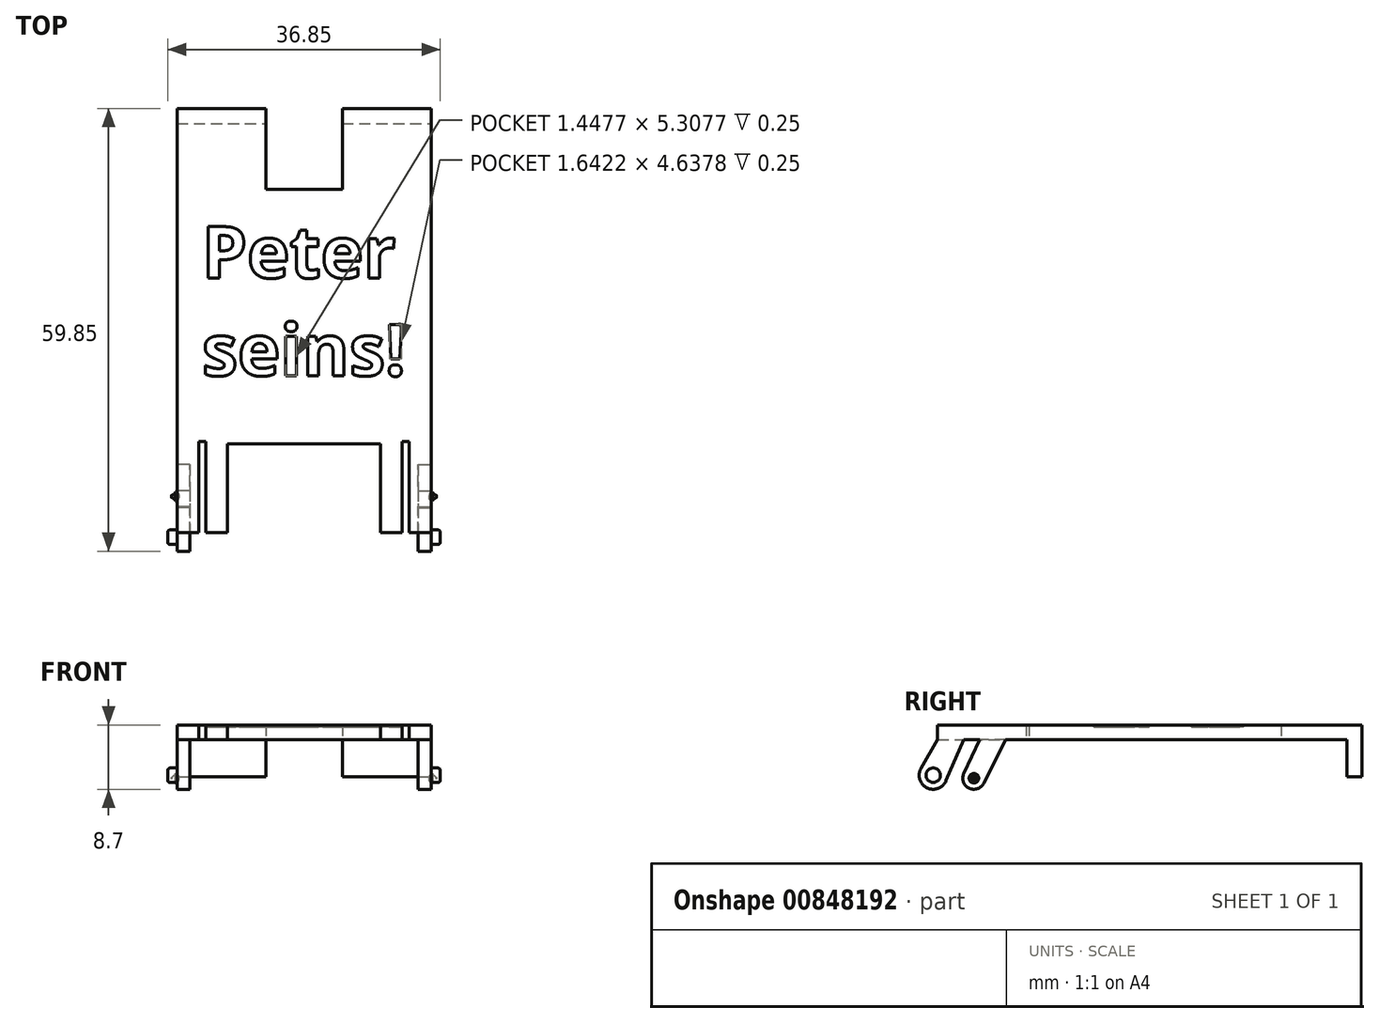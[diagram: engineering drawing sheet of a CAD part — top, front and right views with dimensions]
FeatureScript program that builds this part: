
annotation { "Feature Type Name" : "Feature", "Feature Type Description" : "" }
export const myFeature = defineFeature(function(context is Context, id is Id, definition is map)
    precondition{}
    {
        {
            var Q0;
            Q0=qCreatedBy(makeId("Right.planeOp"),FACE);
            var sketch = newSketch(context, id + "F0", { "sketchPlane" : qUnion([Q0])});
            skLineSegment(sketch, "E0.bottom", {"start": v(25.06, 0) * mm, "end": v(-32.3, 0) * mm});
            skLineSegment(sketch, "E0.top", {"start": v(25.06, -2) * mm, "end": v(-32.3, -2) * mm});
            skLineSegment(sketch, "E0.left", {"start": v(25.06, 0) * mm, "end": v(25.06, -2) * mm});
            skLineSegment(sketch, "E0.right", {"start": v(-32.3, 0) * mm, "end": v(-32.3, -2) * mm});
            skLineSegment(sketch, "E1.bottom", {"start": v(25.06, -2) * mm, "end": v(23.06, -2) * mm});
            skLineSegment(sketch, "E1.top", {"start": v(25.06, 5) * mm, "end": v(23.06, 5) * mm});
            skLineSegment(sketch, "E1.left", {"start": v(25.06, -2) * mm, "end": v(25.06, 5) * mm});
            skLineSegment(sketch, "E1.right", {"start": v(23.06, -2) * mm, "end": v(23.06, 5) * mm});
            skSolve(sketch);
        }
        {
            var Q0;
            Q0 = qSketchRegion(id + "F0", true);
            extrude(context, id + "F1", {"entities" : qUnion([Q0]), "depth" : 34.35 * mm, "offsetDistance" : 25 * mm});
        }
        {
            var Q0;
            Q0=qCreatedBy(makeId("Top.planeOp"),FACE);
            var sketch = newSketch(context, id + "F2", { "sketchPlane" : qUnion([Q0])});
            skLineSegment(sketch, "E2.bottom", {"start": v(6.85, -20.3) * mm, "end": v(27.5, -20.3) * mm});
            skLineSegment(sketch, "E2.top", {"start": v(6.85, -32.4) * mm, "end": v(27.5, -32.4) * mm});
            skLineSegment(sketch, "E2.left", {"start": v(6.85, -20.3) * mm, "end": v(6.85, -32.4) * mm});
            skLineSegment(sketch, "E2.right", {"start": v(27.5, -20.3) * mm, "end": v(27.5, -32.4) * mm});
            skLineSegment(sketch, "E3.bottom", {"start": v(12, 25.16) * mm, "end": v(22.35, 25.16) * mm});
            skLineSegment(sketch, "E3.top", {"start": v(12, 14.16) * mm, "end": v(22.35, 14.16) * mm});
            skLineSegment(sketch, "E3.left", {"start": v(12, 25.16) * mm, "end": v(12, 14.16) * mm});
            skLineSegment(sketch, "E3.right", {"start": v(22.35, 25.16) * mm, "end": v(22.35, 14.16) * mm});
            skLineSegment(sketch, "E4.bottom", {"start": v(2.93, -19.93) * mm, "end": v(3.93, -19.93) * mm});
            skLineSegment(sketch, "E4.top", {"start": v(2.93, -34.8) * mm, "end": v(3.93, -34.8) * mm});
            skLineSegment(sketch, "E4.left", {"start": v(2.93, -19.93) * mm, "end": v(2.93, -34.8) * mm});
            skLineSegment(sketch, "E4.right", {"start": v(3.93, -19.93) * mm, "end": v(3.93, -34.8) * mm});
            skLineSegment(sketch, "E5", {"start": v(17.18, 25.16) * mm, "end": v(17.18, -32.4) * mm, "construction": true});
            skLineSegment(sketch, "E6.MirrorCS", {"start": v(31.43, -19.93) * mm, "end": v(31.43, -34.8) * mm});
            skLineSegment(sketch, "E7.MirrorCS", {"start": v(30.43, -19.93) * mm, "end": v(30.43, -34.8) * mm});
            skLineSegment(sketch, "E8.MirrorCS", {"start": v(31.43, -19.93) * mm, "end": v(30.42, -19.93) * mm});
            skLineSegment(sketch, "E9.MirrorCS", {"start": v(31.43, -34.8) * mm, "end": v(30.42, -34.8) * mm});
            skSolve(sketch);
        }
        {
            var Q0;
            Q0=makeQuery(id+"F2.imprint","IMPRINT",FACE,{"disambiguationData":[TD([[makeQuery(id+"F2.imprint","IMPRINT",EDGE,{"derivedFrom":sQuery(id+"F2.wireOp",EDGE,"E2.bottom")}),-1.0]])]});
            var Q1;
            Q1=makeQuery(id+"F2.imprint","IMPRINT",FACE,{"disambiguationData":[TD([[makeQuery(id+"F2.imprint","IMPRINT",EDGE,{"derivedFrom":sQuery(id+"F2.wireOp",EDGE,"E3.bottom")}),-1.0]])]});
            var Q2;
            Q2=makeQuery(id+"F2.imprint","IMPRINT",FACE,{"disambiguationData":[TD([[makeQuery(id+"F2.imprint","IMPRINT",EDGE,{"derivedFrom":sQuery(id+"F2.wireOp",EDGE,"E4.bottom")}),-1.0]])]});
            var Q3;
            Q3=makeQuery(id+"F2.imprint","IMPRINT",FACE,{"disambiguationData":[TD([[makeQuery(id+"F2.imprint","IMPRINT",EDGE,{"derivedFrom":sQuery(id+"F2.wireOp",EDGE,"E6.MirrorCS")}),-1.0]])]});
            extrude(context, id + "F3", {"entities" : qUnion([Q0, Q1, Q2, Q3]), "operationType" : NewBodyOperationType.REMOVE, "endBound" : BoundingType.SYMMETRIC, "oppositeDirection" : true, "depth" : 25 * mm, "offsetDistance" : 25 * mm});
        }
        {
            var Q0;
            Q0=qCreatedBy(makeId("Right.planeOp"),FACE);
            var sketch = newSketch(context, id + "F4", { "sketchPlane" : qUnion([Q0])});
            skCircle(sketch, "E10", {"center": v(-32.9, 4.8) * mm, "radius": 1.9 * mm});
            skLineSegment(sketch, "E11", {"start": v(-34.53, 3.84) * mm, "end": v(-32.3, 0) * mm});
            skLineSegment(sketch, "E12", {"start": v(-32.3, 0) * mm, "end": v(-28.8, 0) * mm});
            skLineSegment(sketch, "E13", {"start": v(-28.8, 0) * mm, "end": v(-31.14, 5.54) * mm});
            skCircle(sketch, "E14", {"center": v(-32.9, 4.8) * mm, "radius": 1.9 * mm, "construction": true});
            skCircle(sketch, "E15", {"center": v(-27.4, 5.2) * mm, "radius": 1.5 * mm});
            skLineSegment(sketch, "E16", {"start": v(-26.05, 5.87) * mm, "end": v(-23.1, 0) * mm});
            skLineSegment(sketch, "E17", {"start": v(-23.1, 0) * mm, "end": v(-26.6, 0) * mm});
            skLineSegment(sketch, "E18", {"start": v(-26.6, 0) * mm, "end": v(-28.75, 4.56) * mm});
            skCircle(sketch, "E19", {"center": v(-27.4, 5.2) * mm, "radius": 1.5 * mm, "construction": true});
            skSolve(sketch);
        }
        {
            var Q0;
            {var subQ0=sQuery(id+"F4.wireOp",EDGE,"E15");var subQ1=makeQuery(id+"F4.imprint","INTERSECT",VERTEX,{"derivedFrom":[subQ0,sQuery(id+"F4.wireOp",EDGE,"E16")]});Q0=makeQuery(id+"F4.imprint","IMPRINT",FACE,{"disambiguationData":[TD([[makeQuery(id+"F4.imprint","IMPRINT",EDGE,{"disambiguationData":[TD([[subQ1,-1.0]])],"derivedFrom":subQ0}),1.0]])]});}
            var Q1;
            {var subQ0=sQuery(id+"F4.wireOp",EDGE,"E16");Q1=makeQuery(id+"F4.imprint","IMPRINT",FACE,{"disambiguationData":[TD([[makeQuery(id+"F4.imprint","IMPRINT",EDGE,{"derivedFrom":subQ0}),-1.0]])]});}
            var Q2;
            {var subQ0=sQuery(id+"F4.wireOp",EDGE,"E11");Q2=makeQuery(id+"F4.imprint","IMPRINT",FACE,{"disambiguationData":[TD([[makeQuery(id+"F4.imprint","IMPRINT",EDGE,{"derivedFrom":subQ0}),1.0]])]});}
            var Q3;
            {var subQ0=sQuery(id+"F4.wireOp",EDGE,"E10");var subQ1=makeQuery(id+"F4.imprint","INTERSECT",VERTEX,{"derivedFrom":[subQ0,sQuery(id+"F4.wireOp",EDGE,"E11")]});Q3=makeQuery(id+"F4.imprint","IMPRINT",FACE,{"disambiguationData":[TD([[makeQuery(id+"F4.imprint","IMPRINT",EDGE,{"disambiguationData":[TD([[subQ1,1.0]])],"derivedFrom":subQ0}),1.0]])]});}
            extrude(context, id + "F5", {"entities" : qUnion([Q0, Q1, Q2, Q3]), "depth" : 1.75 * mm, "offsetDistance" : 25 * mm});
        }
        {
            var Q0;
            Q0=qCreatedBy(makeId("Right.planeOp"),FACE);
            var sketch = newSketch(context, id + "F6", { "sketchPlane" : qUnion([Q0])});
            skCircle(sketch, "E20", {"center": v(-32.9, 4.8) * mm, "radius": 0.98 * mm});
            skSolve(sketch);
        }
        {
            var Q0;
            Q0=makeQuery(id+"F6.imprint","IMPRINT",FACE,{"disambiguationData":[TD([[makeQuery(id+"F6.imprint","IMPRINT",EDGE,{"derivedFrom":sQuery(id+"F6.wireOp",EDGE,"E20")}),1.0]])]});
            extrude(context, id + "F7", {"entities" : qUnion([Q0]), "oppositeDirection" : true, "depth" : 1.25 * mm, "offsetDistance" : 25 * mm});
        }
        {
            var Q0;
            Q0=qCreatedBy(makeId("Right.planeOp"),FACE);
            var sketch = newSketch(context, id + "F8", { "sketchPlane" : qUnion([Q0])});
            skCircle(sketch, "E21", {"center": v(-27.4, 5.2) * mm, "radius": 0.65 * mm});
            skSolve(sketch);
        }
        {
            var Q0;
            Q0=makeQuery(id+"F8.imprint","IMPRINT",FACE,{"disambiguationData":[TD([[makeQuery(id+"F8.imprint","IMPRINT",EDGE,{"derivedFrom":sQuery(id+"F8.wireOp",EDGE,"E21")}),1.0]])]});
            extrude(context, id + "F9", {"entities" : qUnion([Q0]), "oppositeDirection" : true, "depth" : 0.75 * mm, "offsetDistance" : 25 * mm});
        }
        {
            var Q0;
            Q0=makeQuery(id+"F9.opExtrude","CAP_EDGE",EDGE,{"disambiguationData":[OSD([sQuery(id+"F8.wireOp",EDGE,"E21")])],"isStart":false});
            fillet(context, id + "F10", {"entities" : qUnion([Q0]), "radius" : 0.5 * mm, "tangentPropagation" : true, "allowEdgeOverflow" : false});
        }
        {
            var Q0;
            Q0=makeQuery(id+"F7.opExtrude","CAP_EDGE",EDGE,{"disambiguationData":[OSD([sQuery(id+"F6.wireOp",EDGE,"E20")])],"isStart":false});
            fillet(context, id + "F11", {"entities" : qUnion([Q0]), "radius" : 0.3 * mm, "tangentPropagation" : true, "allowEdgeOverflow" : false});
        }
        {
            var Q0;
            Q0=qCreatedBy(makeId("Right.planeOp"),FACE);
            cPlane(context, id + "F12", {"entities" : qUnion([Q0]), "cplaneType" : CPlaneType.OFFSET, "offset" : (34.35 / 2) * mm, "width" : 150 * mm, "height" : 150 * mm});
        }
        {
            var Q0;
            Q0=makeQuery(id+"F9.opExtrude","SWEPT_BODY",BODY,{"disambiguationData":[OSD([sQuery(id+"F8.wireOp",EDGE,"E21")])]});
            var Q1;
            Q1=makeQuery(id+"F5.opExtrude","SWEPT_BODY",BODY,{"disambiguationData":[OSD([sQuery(id+"F4.wireOp",EDGE,"E15"),sQuery(id+"F4.wireOp",EDGE,"E16"),sQuery(id+"F4.wireOp",EDGE,"E17"),sQuery(id+"F4.wireOp",EDGE,"E18")])]});
            var Q2;
            Q2=makeQuery(id+"F7.opExtrude","SWEPT_BODY",BODY,{"disambiguationData":[OSD([sQuery(id+"F6.wireOp",EDGE,"E20")])]});
            var Q3;
            Q3=makeQuery(id+"F5.opExtrude","SWEPT_BODY",BODY,{"disambiguationData":[OSD([sQuery(id+"F4.wireOp",EDGE,"E10"),sQuery(id+"F4.wireOp",EDGE,"E11"),sQuery(id+"F4.wireOp",EDGE,"E12"),sQuery(id+"F4.wireOp",EDGE,"E13")])]});
            var Q4;
            Q4=qCreatedBy(id+"F12.planeOp",FACE);
            mirror(context, id + "F13", {"operationType" : NewBodyOperationType.ADD, "entities" : qUnion([Q0, Q1, Q2, Q3]), "mirrorPlane" : qUnion([Q4])});
        }
        {
            var Q0;
            Q0=makeQuery(id+"F1.opExtrude","SWEPT_BODY",BODY,{"disambiguationData":[OSD([sQuery(id+"F0.wireOp",EDGE,"E0.bottom"),sQuery(id+"F0.wireOp",EDGE,"E0.top"),sQuery(id+"F0.wireOp",EDGE,"E0.right"),sQuery(id+"F0.wireOp",EDGE,"E1.bottom"),sQuery(id+"F0.wireOp",EDGE,"E1.top"),sQuery(id+"F0.wireOp",EDGE,"E1.left"),sQuery(id+"F0.wireOp",EDGE,"E1.right")])]});
            var Q1;
            {var subQ0=sQuery(id+"F0.wireOp",EDGE,"E1.right");var subQ1=sQuery(id+"F0.wireOp",EDGE,"E0.bottom");Q1=makeQuery(id+"F13.boolean.opBoolean","SPLIT",EDGE,{"disambiguationData":[TD([makeQuery(id+"F1.opExtrude","SWEPT_FACE",FACE,{"disambiguationData":[OSD([subQ0])]})])],"derivedFrom":makeQuery(id+"F1.opExtrude","CAP_EDGE",EDGE,{"disambiguationData":[OSD([subQ1])],"isStart":true})});}
            transform(context, id + "F14", {"entities" : qUnion([Q0]), "transformType" : TransformType.ROTATION, "transformAxis" : qUnion([Q1]), "angle" : 180 * degree, "makeCopy" : false});
        }
        {
            var Q0;
            Q0=makeQuery(id+"F1.opExtrude","SWEPT_FACE",FACE,{"disambiguationData":[OSD([sQuery(id+"F0.wireOp",EDGE,"E0.top"),sQuery(id+"F0.wireOp",EDGE,"E1.bottom")])]});
            var sketch = newSketch(context, id + "F15", { "sketchPlane" : qUnion([Q0])});
            skText(sketch, "E22", { "text": "Peter\nseins!", "fontName": "OpenSans-Bold.ttf"});
            const initialGuessF15  = {"E22": [-0.03098, 0.00216, 1, 0, 0.007]};
            skSetInitialGuess(sketch, initialGuessF15);
            skSolve(sketch);
        }
        {
            var Q0;
            Q0 = qSketchRegion(id + "F15", true);
            extrude(context, id + "F16", {"entities" : qUnion([Q0]), "operationType" : NewBodyOperationType.REMOVE, "endBound" : BoundingType.SYMMETRIC, "oppositeDirection" : true, "depth" : 0.5 * mm, "offsetDistance" : 25 * mm});
        }
    });
